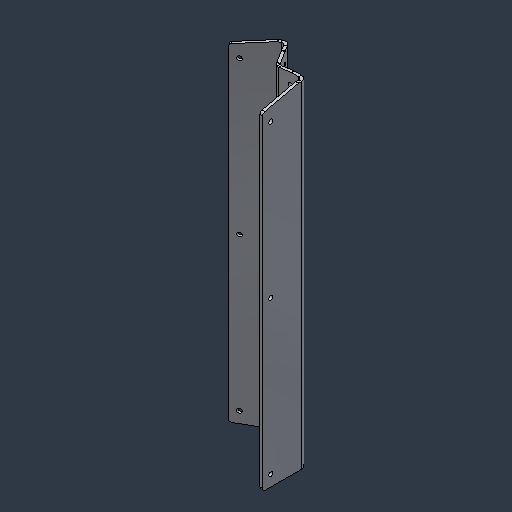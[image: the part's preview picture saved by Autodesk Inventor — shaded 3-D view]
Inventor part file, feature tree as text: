
AUTODESK INVENTOR PART (.ipt)
format: ipt  version: 2024.3 (Build 283343000, 343)  size: 133,120 bytes
history: native  units: mm (DEFAULTED — no unit token found)
features: fillet x1
ambient origin geometry x8: Origin, YZ Plane, XZ Plane, XY Plane, X Axis, Y Axis, Z Axis, Center Point
bodies: Solid1 (feature_tree)
feature tree (1):
  fillet  "Fillet2"  [1 undecoded]
note: 1 required parameter value undecoded (feature->parameter linkage not recoverable at this tier; creation-order binding heuristic only, values carry confidence <= 0.55)
